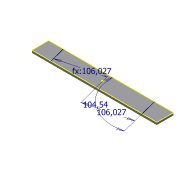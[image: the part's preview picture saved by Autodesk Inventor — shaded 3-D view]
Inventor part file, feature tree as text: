
AUTODESK INVENTOR PART (.ipt)
format: ipt  version: 2016 SP2 (Build 200236200, 236)  size: 121,344 bytes
history: native  units: mm
features: sketch x2, other x2, extrude x1, projected_geometry x1
ambient origin geometry x8: Origin, YZ Plane, XZ Plane, XY Plane, X Axis, Y Axis, Z Axis, Center Point
bodies: Body1 (feature_tree)
feature tree (6):
  extrude  "Extrusion3"  Depth=40.0mm
  sketch  "Sketch2"  dims[d7=250.0mm d8=71.0mm d9=71.0mm d10=13.613568mm d11=2.0mm d12=90.0deg d13=2.0mm d14=90.0deg]
  other  "Bend Part1"
  other  "Bend Part2"
  sketch  "Sketch1"  dims[d4=6.0mm d5=0.0mm d6=40.0mm]
  projected_geometry  "Projected Loop1"
